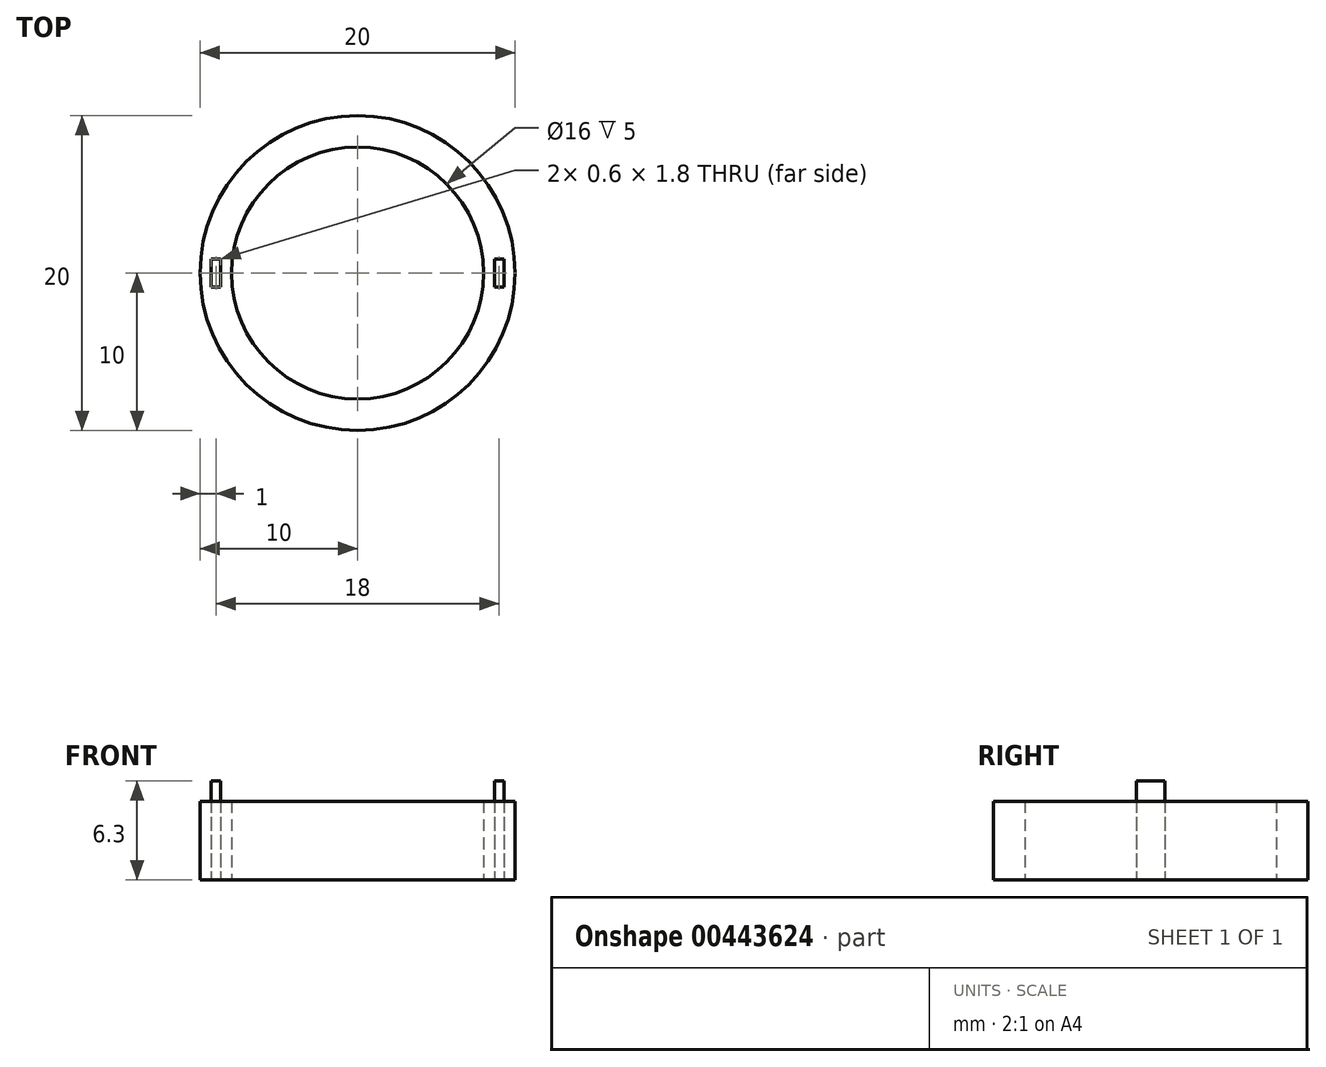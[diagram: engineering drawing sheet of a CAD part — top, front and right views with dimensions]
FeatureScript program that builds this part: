
annotation { "Feature Type Name" : "Feature", "Feature Type Description" : "" }
export const myFeature = defineFeature(function(context is Context, id is Id, definition is map)
    precondition{}
    {
        {
            var Q0;
            Q0=qCreatedBy(makeId("Top.planeOp"),FACE);
            var sketch = newSketch(context, id + "F0", { "sketchPlane" : qUnion([Q0])});
            skCircle(sketch, "E0", {"center": v(0, 0) * mm, "radius": 10 * mm});
            skLineSegment(sketch, "E1.bottom", {"start": v(-9.3, 0.9) * mm, "end": v(-8.7, 0.9) * mm});
            skLineSegment(sketch, "E1.top", {"start": v(-9.3, -0.9) * mm, "end": v(-8.7, -0.9) * mm});
            skLineSegment(sketch, "E1.left", {"start": v(-9.3, 0.9) * mm, "end": v(-9.3, -0.9) * mm});
            skLineSegment(sketch, "E1.right", {"start": v(-8.7, 0.9) * mm, "end": v(-8.7, -0.9) * mm});
            skLineSegment(sketch, "E2.bottom", {"start": v(8.7, 0.9) * mm, "end": v(9.3, 0.9) * mm});
            skLineSegment(sketch, "E2.top", {"start": v(8.7, -0.9) * mm, "end": v(9.3, -0.9) * mm});
            skLineSegment(sketch, "E2.left", {"start": v(8.7, 0.9) * mm, "end": v(8.7, -0.9) * mm});
            skLineSegment(sketch, "E2.right", {"start": v(9.3, 0.9) * mm, "end": v(9.3, -0.9) * mm});
            skCircle(sketch, "E3", {"center": v(0, 0) * mm, "radius": 8 * mm});
            skSolve(sketch);
        }
        {
            var Q0;
            Q0=makeQuery(id+"F0.imprint","IMPRINT",FACE,{"disambiguationData":[TD([[makeQuery(id+"F0.imprint","IMPRINT",EDGE,{"derivedFrom":sQuery(id+"F0.wireOp",EDGE,"E1.bottom")}),-1.0]])]});
            var Q1;
            Q1=makeQuery(id+"F0.imprint","IMPRINT",FACE,{"disambiguationData":[TD([[makeQuery(id+"F0.imprint","IMPRINT",EDGE,{"derivedFrom":sQuery(id+"F0.wireOp",EDGE,"E2.bottom")}),-1.0]])]});
            extrude(context, id + "F1", {"entities" : qUnion([Q0, Q1]), "depth" : 6.3 * mm});
        }
        {
            var Q0;
            Q0 = qSketchRegion(id + "F0", true);
            extrude(context, id + "F2", {"entities" : qUnion([Q0]), "depth" : 5 * mm});
        }
    });
